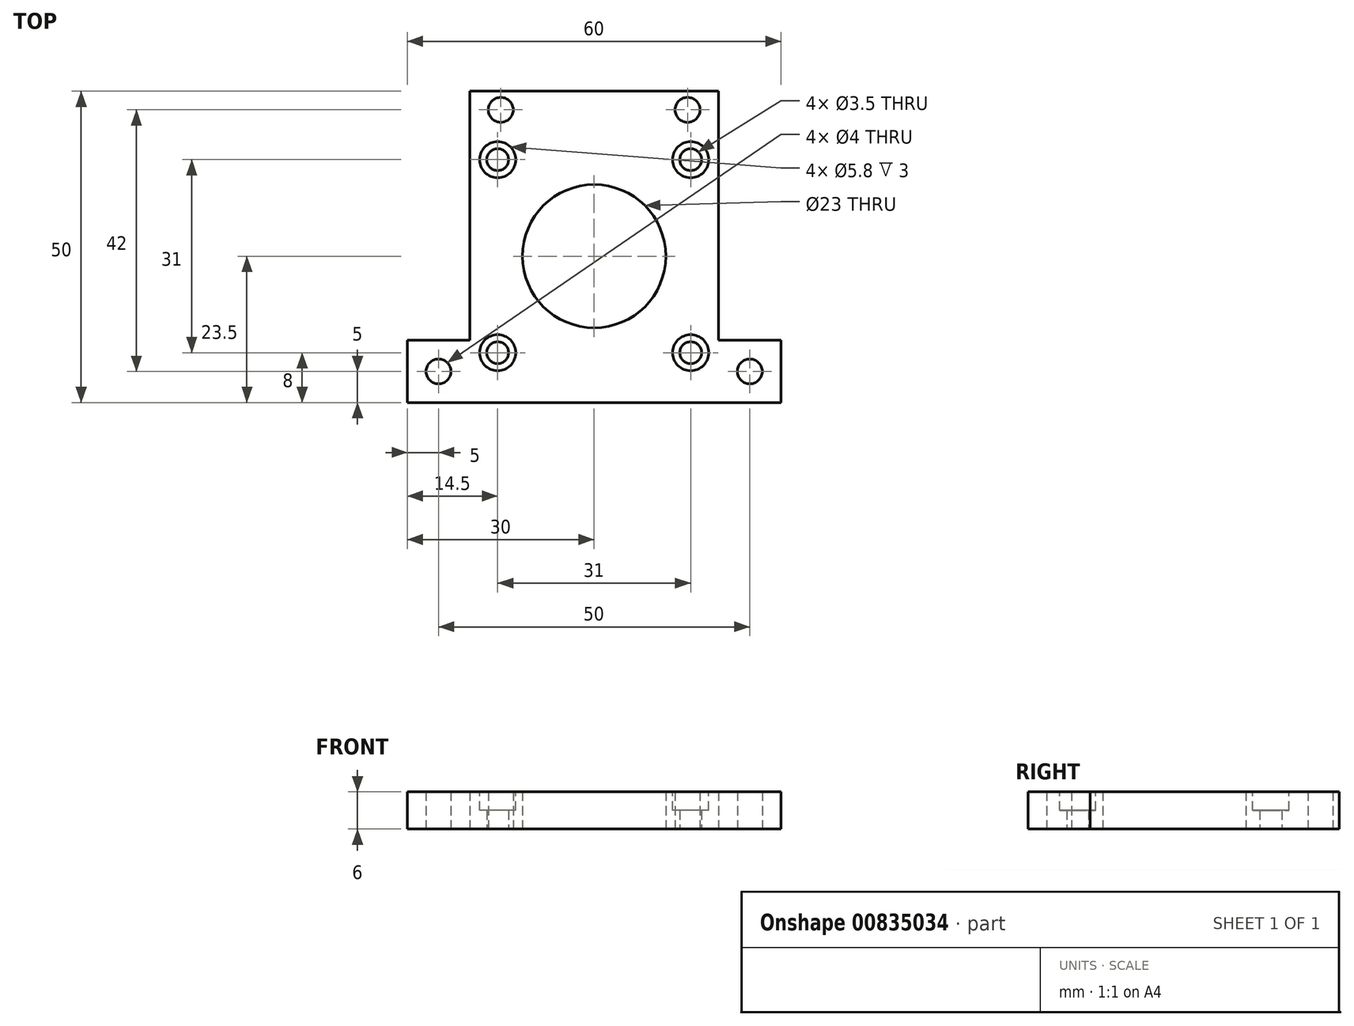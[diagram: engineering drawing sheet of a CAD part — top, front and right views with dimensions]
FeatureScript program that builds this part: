
annotation { "Feature Type Name" : "Feature", "Feature Type Description" : "" }
export const myFeature = defineFeature(function(context is Context, id is Id, definition is map)
    precondition{}
    {
        {
            var Q0;
            Q0=qCreatedBy(makeId("Top.planeOp"),FACE);
            var sketch = newSketch(context, id + "F0", { "sketchPlane" : qUnion([Q0])});
            skLineSegment(sketch, "E0.bottom", {"start": v(20, -23.5) * mm, "end": v(-20, -23.5) * mm});
            skLineSegment(sketch, "E0.top", {"start": v(20, 26.5) * mm, "end": v(-20, 26.5) * mm});
            skLineSegment(sketch, "E0.left", {"start": v(20, -13.5) * mm, "end": v(20, 26.5) * mm});
            skLineSegment(sketch, "E0.right", {"start": v(-20, -13.5) * mm, "end": v(-20, 26.5) * mm});
            skPoint(sketch, "E0.middle", {"position": v(0, 0) * mm});
            skLineSegment(sketch, "E1.bottom", {"start": v(-20, -23.5) * mm, "end": v(-30, -23.5) * mm});
            skLineSegment(sketch, "E1.top", {"start": v(-20, -13.5) * mm, "end": v(-30, -13.5) * mm});
            skLineSegment(sketch, "E1.right", {"start": v(-30, -23.5) * mm, "end": v(-30, -13.5) * mm});
            skLineSegment(sketch, "E2.bottom", {"start": v(20, -23.5) * mm, "end": v(30, -23.5) * mm});
            skLineSegment(sketch, "E2.top", {"start": v(20, -13.5) * mm, "end": v(30, -13.5) * mm});
            skLineSegment(sketch, "E2.right", {"start": v(30, -23.5) * mm, "end": v(30, -13.5) * mm});
            skCircle(sketch, "E3", {"center": v(0, 0) * mm, "radius": 11.5 * mm});
            skLineSegment(sketch, "E4.bottom", {"start": v(15.5, -15.5) * mm, "end": v(-15.5, -15.5) * mm, "construction": true});
            skLineSegment(sketch, "E4.top", {"start": v(15.5, 15.5) * mm, "end": v(-15.5, 15.5) * mm, "construction": true});
            skLineSegment(sketch, "E4.left", {"start": v(15.5, -15.5) * mm, "end": v(15.5, 15.5) * mm, "construction": true});
            skLineSegment(sketch, "E4.right", {"start": v(-15.5, -15.5) * mm, "end": v(-15.5, 15.5) * mm, "construction": true});
            skCircle(sketch, "E5", {"center": v(-15.5, 15.5) * mm, "radius": 1.75 * mm});
            skCircle(sketch, "E6", {"center": v(-25, -18.5) * mm, "radius": 2 * mm});
            skPoint(sketch, "E6.centerSnap0", {"position": v(-30, -18.5) * mm});
            skCircle(sketch, "E7", {"center": v(25, -18.5) * mm, "radius": 2 * mm});
            skCircle(sketch, "E8.1.0", {"center": v(-15.5, -15.5) * mm, "radius": 1.75 * mm});
            skCircle(sketch, "E8.2.0", {"center": v(15.5, -15.5) * mm, "radius": 1.75 * mm});
            skCircle(sketch, "E8.3.0", {"center": v(15.5, 15.5) * mm, "radius": 1.75 * mm});
            skCircle(sketch, "E9", {"center": v(-15, 23.5) * mm, "radius": 2 * mm});
            skCircle(sketch, "E10", {"center": v(15, 23.5) * mm, "radius": 2 * mm});
            skSolve(sketch);
        }
        {
            var Q0;
            Q0=makeQuery(id+"F0.imprint","IMPRINT",FACE,{"disambiguationData":[TD([[makeQuery(id+"F0.imprint","IMPRINT",EDGE,{"derivedFrom":sQuery(id+"F0.wireOp",EDGE,"E0.bottom")}),-1.0]])]});
            extrude(context, id + "F1", {"entities" : qUnion([Q0]), "depth" : 6 * mm, "offsetDistance" : 25 * mm});
        }
        {
            var Q0;
            Q0=makeQuery(id+"F1.opExtrude","CAP_FACE",FACE,{"disambiguationData":[OSD([sQuery(id+"F0.wireOp",EDGE,"E0.bottom"),sQuery(id+"F0.wireOp",EDGE,"E0.top"),sQuery(id+"F0.wireOp",EDGE,"E0.left"),sQuery(id+"F0.wireOp",EDGE,"E0.right"),sQuery(id+"F0.wireOp",EDGE,"E1.bottom"),sQuery(id+"F0.wireOp",EDGE,"E1.top"),sQuery(id+"F0.wireOp",EDGE,"E1.right"),sQuery(id+"F0.wireOp",EDGE,"E2.bottom"),sQuery(id+"F0.wireOp",EDGE,"E2.top"),sQuery(id+"F0.wireOp",EDGE,"E2.right"),sQuery(id+"F0.wireOp",EDGE,"E3"),sQuery(id+"F0.wireOp",EDGE,"E5"),sQuery(id+"F0.wireOp",EDGE,"E6"),sQuery(id+"F0.wireOp",EDGE,"E7"),sQuery(id+"F0.wireOp",EDGE,"E8.1.0"),sQuery(id+"F0.wireOp",EDGE,"E8.2.0"),sQuery(id+"F0.wireOp",EDGE,"E8.3.0"),sQuery(id+"F0.wireOp",EDGE,"E9"),sQuery(id+"F0.wireOp",EDGE,"E10")])],"isStart":false});
            var sketch = newSketch(context, id + "F2", { "sketchPlane" : qUnion([Q0])});
            skCircle(sketch, "E11", {"center": v(-15.5, 15.5) * mm, "radius": 2.9 * mm});
            skCircle(sketch, "E12.1.0", {"center": v(-15.5, -15.5) * mm, "radius": 2.9 * mm});
            skCircle(sketch, "E12.2.0", {"center": v(15.5, -15.5) * mm, "radius": 2.9 * mm});
            skCircle(sketch, "E12.3.0", {"center": v(15.5, 15.5) * mm, "radius": 2.9 * mm});
            skPoint(sketch, "E12.center", {"position": v(0, 0) * mm});
            skSolve(sketch);
        }
        {
            var Q0;
            Q0=makeQuery(id+"F2.imprint","IMPRINT",FACE,{"disambiguationData":[TD([[makeQuery(id+"F2.imprint","IMPRINT",EDGE,{"derivedFrom":sQuery(id+"F2.wireOp",EDGE,"E11")}),1.0]])]});
            var Q1;
            Q1=makeQuery(id+"F2.imprint","IMPRINT",FACE,{"disambiguationData":[TD([[makeQuery(id+"F2.imprint","IMPRINT",EDGE,{"derivedFrom":sQuery(id+"F2.wireOp",EDGE,"E12.3.0")}),1.0]])]});
            var Q2;
            Q2=makeQuery(id+"F2.imprint","IMPRINT",FACE,{"disambiguationData":[TD([[makeQuery(id+"F2.imprint","IMPRINT",EDGE,{"derivedFrom":sQuery(id+"F2.wireOp",EDGE,"E12.2.0")}),1.0]])]});
            var Q3;
            Q3=makeQuery(id+"F2.imprint","IMPRINT",FACE,{"disambiguationData":[TD([[makeQuery(id+"F2.imprint","IMPRINT",EDGE,{"derivedFrom":sQuery(id+"F2.wireOp",EDGE,"E12.1.0")}),1.0]])]});
            extrude(context, id + "F3", {"entities" : qUnion([Q0, Q1, Q2, Q3]), "operationType" : NewBodyOperationType.REMOVE, "oppositeDirection" : true, "depth" : 3 * mm, "offsetDistance" : 25 * mm});
        }
    });
